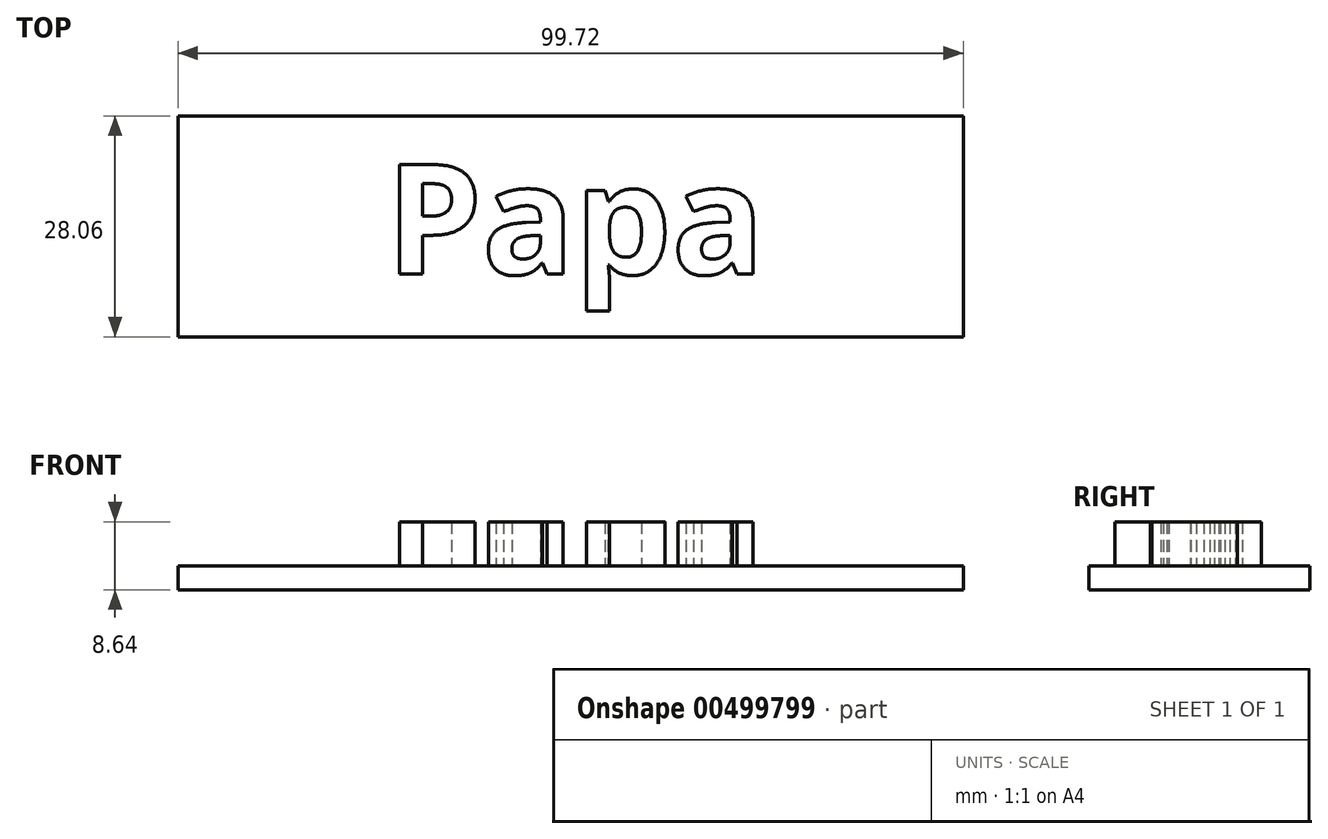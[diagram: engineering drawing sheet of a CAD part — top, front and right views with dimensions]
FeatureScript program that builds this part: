
annotation { "Feature Type Name" : "Feature", "Feature Type Description" : "" }
export const myFeature = defineFeature(function(context is Context, id is Id, definition is map)
    precondition{}
    {
        {
            var Q0;
            Q0=qCreatedBy(makeId("Top.planeOp"),FACE);
            var sketch = newSketch(context, id + "F0", { "sketchPlane" : qUnion([Q0])});
            skLineSegment(sketch, "E0.bottom", {"start": v(-49.86, 14.03) * mm, "end": v(49.86, 14.03) * mm});
            skLineSegment(sketch, "E0.top", {"start": v(-49.86, -14.03) * mm, "end": v(49.86, -14.03) * mm});
            skLineSegment(sketch, "E0.left", {"start": v(-49.86, 14.03) * mm, "end": v(-49.86, -14.03) * mm});
            skLineSegment(sketch, "E0.right", {"start": v(49.86, 14.03) * mm, "end": v(49.86, -14.03) * mm});
            skPoint(sketch, "E0.middle", {"position": v(0, 0) * mm});
            skSolve(sketch);
        }
        {
            var Q0;
            Q0 = qSketchRegion(id + "F0", true);
            extrude(context, id + "F1", {"entities" : qUnion([Q0]), "depth" : 3.05 * mm});
        }
        {
            var Q0;
            Q0=makeQuery(id+"F1.opExtrude","CAP_FACE",FACE,{"disambiguationData":[OSD([sQuery(id+"F0.wireOp",EDGE,"E0.bottom"),sQuery(id+"F0.wireOp",EDGE,"E0.top"),sQuery(id+"F0.wireOp",EDGE,"E0.left"),sQuery(id+"F0.wireOp",EDGE,"E0.right")])],"isStart":false});
            var sketch = newSketch(context, id + "F2", { "sketchPlane" : qUnion([Q0])});
            skText(sketch, "E1", { "text": "Papa", "fontName": "OpenSans-Bold.ttf"});
            const initialGuessF2  = {"E1": [-0.02351, -0.00607, 1, 0, 0.01403]};
            skSetInitialGuess(sketch, initialGuessF2);
            skSolve(sketch);
        }
        {
            var Q0;
            Q0 = qSketchRegion(id + "F2", true);
            extrude(context, id + "F3", {"entities" : qUnion([Q0]), "operationType" : NewBodyOperationType.ADD, "depth" : 5.6 * mm});
        }
    });
